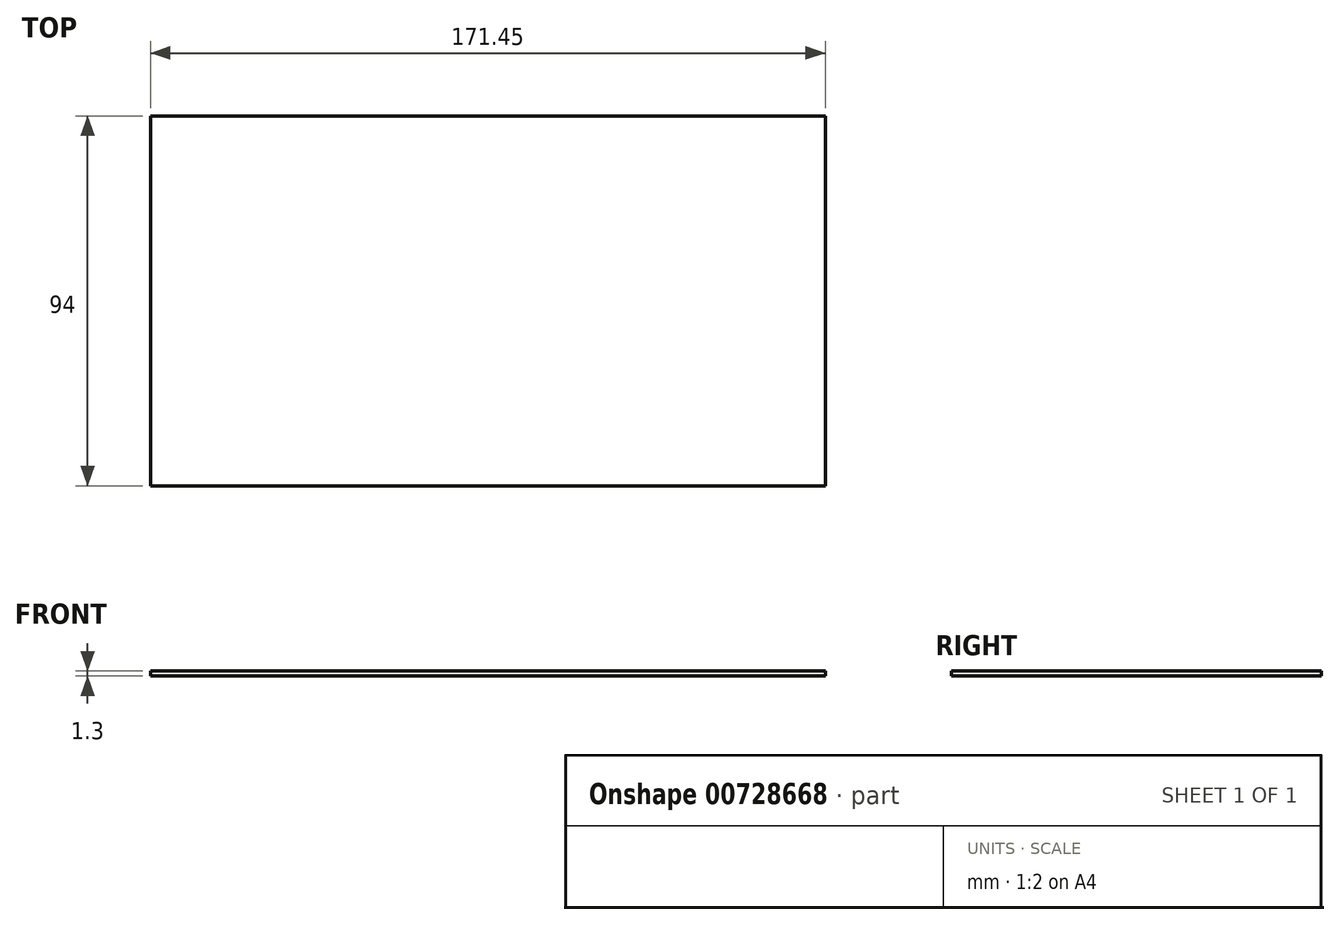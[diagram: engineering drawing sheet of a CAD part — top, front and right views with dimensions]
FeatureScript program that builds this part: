
annotation { "Feature Type Name" : "Feature", "Feature Type Description" : "" }
export const myFeature = defineFeature(function(context is Context, id is Id, definition is map)
    precondition{}
    {
        {
            var Q0;
            Q0=qCreatedBy(makeId("Top.planeOp"),FACE);
            var sketch = newSketch(context, id + "F0", { "sketchPlane" : qUnion([Q0])});
            skLineSegment(sketch, "E0.bottom", {"start": v(-73.72, 13.67) * mm, "end": v(97.73, 13.67) * mm});
            skLineSegment(sketch, "E0.top", {"start": v(-73.72, -80.33) * mm, "end": v(97.73, -80.33) * mm});
            skLineSegment(sketch, "E0.left", {"start": v(-73.72, 13.67) * mm, "end": v(-73.72, -80.33) * mm});
            skLineSegment(sketch, "E0.right", {"start": v(97.73, 13.67) * mm, "end": v(97.73, -80.33) * mm});
            skSolve(sketch);
        }
        {
            var Q0;
            Q0=makeQuery(id+"F0.imprint","IMPRINT",FACE,{"disambiguationData":[TD([[makeQuery(id+"F0.imprint","IMPRINT",EDGE,{"derivedFrom":sQuery(id+"F0.wireOp",EDGE,"E0.bottom")}),-1.0]])]});
            extrude(context, id + "F1", {"entities" : qUnion([Q0]), "depth" : 1.3 * mm, "offsetDistance" : 25.4 * mm});
        }
    });
